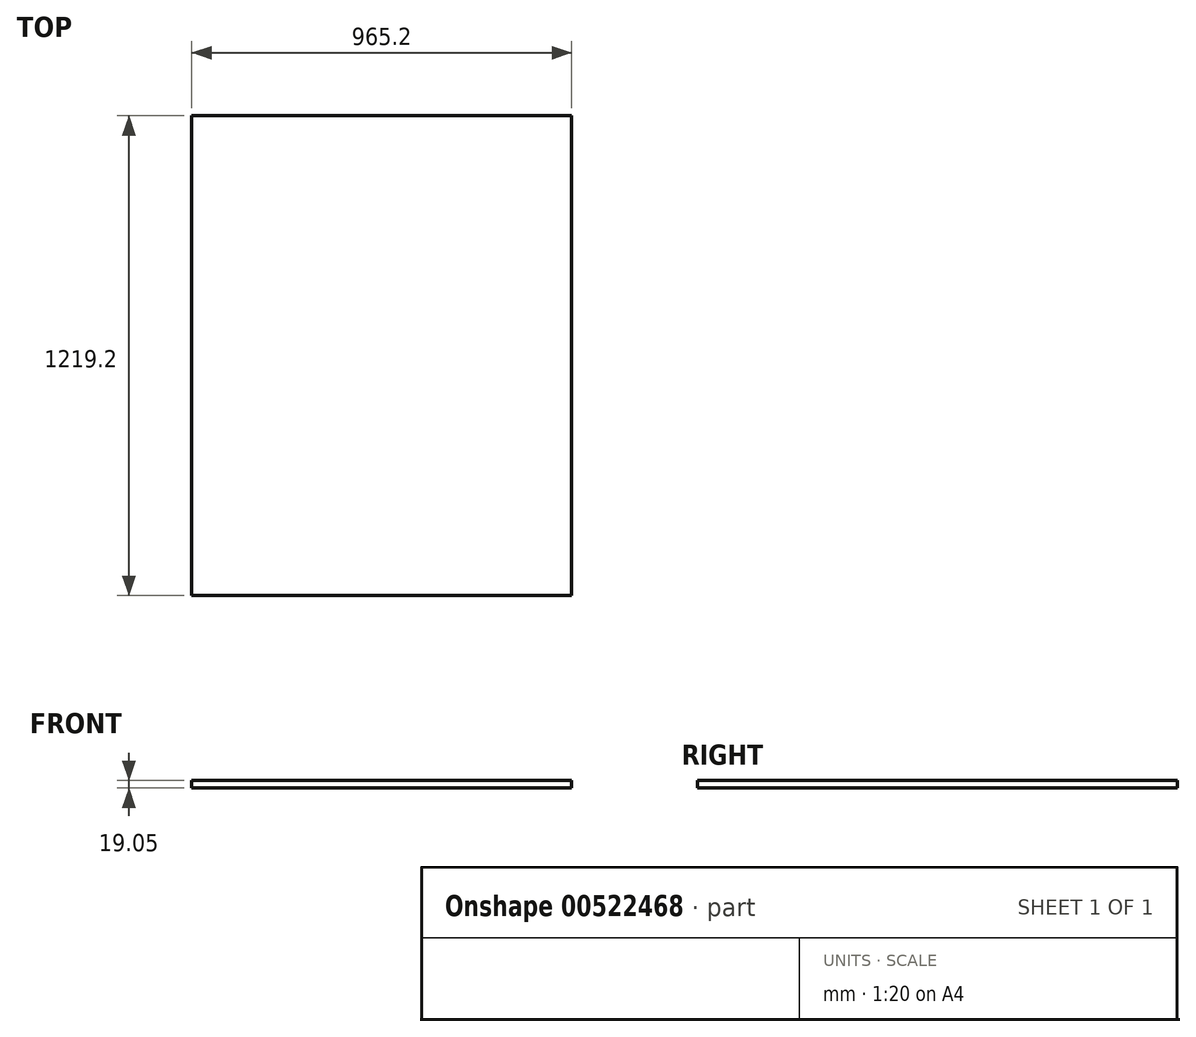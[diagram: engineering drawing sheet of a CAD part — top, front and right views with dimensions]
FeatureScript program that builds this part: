
annotation { "Feature Type Name" : "Feature", "Feature Type Description" : "" }
export const myFeature = defineFeature(function(context is Context, id is Id, definition is map)
    precondition{}
    {
        {
            var Q0;
            Q0=qCreatedBy(makeId("Top.planeOp"),FACE);
            var sketch = newSketch(context, id + "F0", { "sketchPlane" : qUnion([Q0])});
            skLineSegment(sketch, "E0.bottom", {"start": v(-340.75, 817.88) * mm, "end": v(624.45, 817.88) * mm});
            skLineSegment(sketch, "E0.top", {"start": v(-340.75, -401.32) * mm, "end": v(624.45, -401.32) * mm});
            skLineSegment(sketch, "E0.left", {"start": v(-340.75, 817.88) * mm, "end": v(-340.75, -401.32) * mm});
            skLineSegment(sketch, "E0.right", {"start": v(624.45, 817.88) * mm, "end": v(624.45, -401.32) * mm});
            skSolve(sketch);
        }
        {
            var Q0;
            Q0=makeQuery(id+"F0.imprint","IMPRINT",FACE,{"disambiguationData":[TD([[makeQuery(id+"F0.imprint","IMPRINT",EDGE,{"derivedFrom":sQuery(id+"F0.wireOp",EDGE,"E0.bottom")}),-1.0]])]});
            extrude(context, id + "F1", {"entities" : qUnion([Q0]), "depth" : 19.05 * mm, "offsetDistance" : 25.4 * mm});
        }
    });
